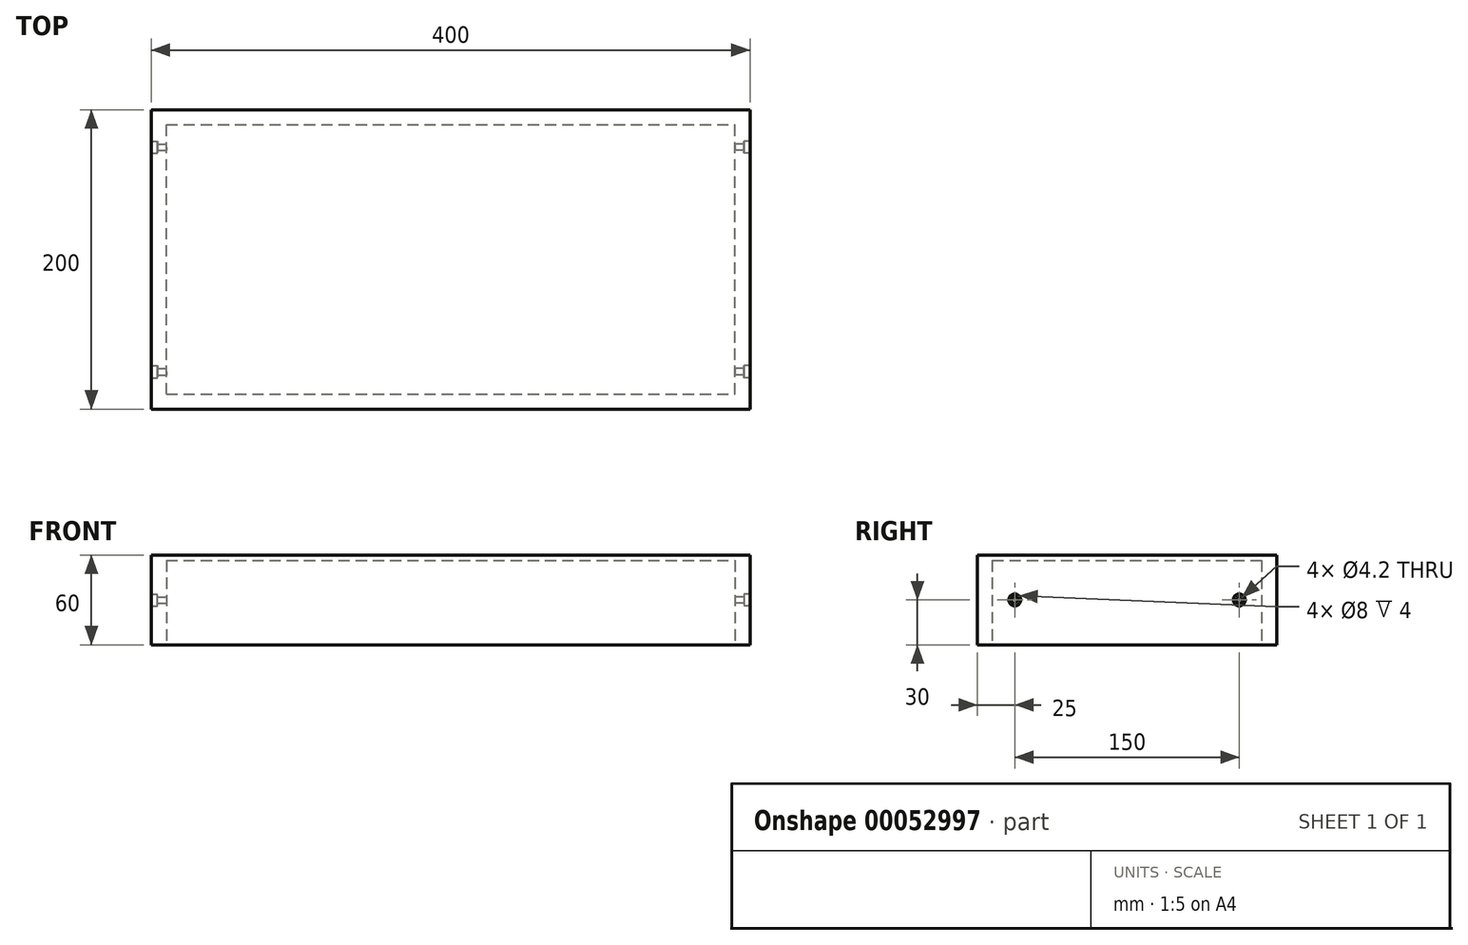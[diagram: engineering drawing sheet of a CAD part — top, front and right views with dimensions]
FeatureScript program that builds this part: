
annotation { "Feature Type Name" : "Feature", "Feature Type Description" : "" }
export const myFeature = defineFeature(function(context is Context, id is Id, definition is map)
    precondition{}
    {
        {
            var Q0;
            Q0=qCreatedBy(makeId("Top.planeOp"),FACE);
            var sketch = newSketch(context, id + "F0", { "sketchPlane" : qUnion([Q0])});
            skLineSegment(sketch, "E0.bottom", {"start": v(-200, 100) * mm, "end": v(200, 100) * mm});
            skLineSegment(sketch, "E0.top", {"start": v(-200, -100) * mm, "end": v(200, -100) * mm});
            skLineSegment(sketch, "E0.left", {"start": v(-200, 100) * mm, "end": v(-200, -100) * mm});
            skLineSegment(sketch, "E0.right", {"start": v(200, 100) * mm, "end": v(200, -100) * mm});
            skSolve(sketch);
        }
        {
            var Q0;
            Q0=makeQuery(id+"F0.imprint","IMPRINT",FACE,{"disambiguationData":[TD([[makeQuery(id+"F0.imprint","IMPRINT",EDGE,{"derivedFrom":sQuery(id+"F0.wireOp",EDGE,"E0.bottom")}),-1.0]])]});
            extrude(context, id + "F1", {"entities" : qUnion([Q0]), "oppositeDirection" : true, "depth" : 3.6 * mm});
        }
        {
            var Q0;
            Q0=makeQuery(id+"F1.opExtrude","CAP_FACE",FACE,{"disambiguationData":[OSD([sQuery(id+"F0.wireOp",EDGE,"E0.bottom"),sQuery(id+"F0.wireOp",EDGE,"E0.top"),sQuery(id+"F0.wireOp",EDGE,"E0.left"),sQuery(id+"F0.wireOp",EDGE,"E0.right")])],"isStart":true});
            cPlane(context, id + "F2", {"entities" : qUnion([Q0]), "cplaneType" : CPlaneType.OFFSET, "offset" : 60 * mm, "oppositeDirection" : true, "width" : 150 * mm, "height" : 150 * mm});
        }
        {
            var Q0;
            Q0=qCreatedBy(id+"F2.planeOp",FACE);
            var sketch = newSketch(context, id + "F3", { "sketchPlane" : qUnion([Q0])});
            skLineSegment(sketch, "E1.0", {"start": v(-200, 100) * mm, "end": v(-200, -100) * mm});
            skLineSegment(sketch, "E2.0", {"start": v(-200, -100) * mm, "end": v(200, -100) * mm});
            skLineSegment(sketch, "E3.0", {"start": v(200, 100) * mm, "end": v(200, -100) * mm});
            skLineSegment(sketch, "E4.0", {"start": v(-200, 100) * mm, "end": v(200, 100) * mm});
            skLineSegment(sketch, "E5.bottom", {"start": v(-190, -90) * mm, "end": v(190, -90) * mm});
            skLineSegment(sketch, "E5.top", {"start": v(-190, 90) * mm, "end": v(190, 90) * mm});
            skLineSegment(sketch, "E5.left", {"start": v(-190, -90) * mm, "end": v(-190, 90) * mm});
            skLineSegment(sketch, "E5.right", {"start": v(190, -90) * mm, "end": v(190, 90) * mm});
            skLineSegment(sketch, "E6", {"start": v(-190, -90) * mm, "end": v(-200, -90) * mm, "construction": true});
            skLineSegment(sketch, "E7", {"start": v(-190, -90) * mm, "end": v(-190, -100) * mm, "construction": true});
            skLineSegment(sketch, "E8", {"start": v(190, 90) * mm, "end": v(200, 90) * mm, "construction": true});
            skLineSegment(sketch, "E9", {"start": v(190, 90) * mm, "end": v(190, 100) * mm, "construction": true});
            skSolve(sketch);
        }
        {
            var Q0;
            Q0=makeQuery(id+"F3.imprint","IMPRINT",FACE,{"disambiguationData":[TD([[makeQuery(id+"F3.imprint","IMPRINT",EDGE,{"derivedFrom":sQuery(id+"F3.wireOp",EDGE,"E1.0")}),1.0]])]});
            var Q1;
            Q1=makeQuery(id+"F1.opExtrude","CAP_FACE",FACE,{"disambiguationData":[OSD([sQuery(id+"F0.wireOp",EDGE,"E0.bottom"),sQuery(id+"F0.wireOp",EDGE,"E0.top"),sQuery(id+"F0.wireOp",EDGE,"E0.left"),sQuery(id+"F0.wireOp",EDGE,"E0.right")])],"isStart":false});
            extrude(context, id + "F4", {"entities" : qUnion([Q0]), "operationType" : NewBodyOperationType.ADD, "endBound" : BoundingType.UP_TO_SURFACE, "endBoundEntityFace" : qUnion([Q1]), "depth" : 25 * mm});
        }
        {
            var Q0;
            Q0=makeQuery(id+"F4.boolean.opBoolean","MERGE",FACE,{"derivedFrom":[makeQuery(id+"F1.opExtrude","SWEPT_FACE",FACE,{"disambiguationData":[OSD([sQuery(id+"F0.wireOp",EDGE,"E0.right")])]}),makeQuery(id+"F4.opExtrude","SWEPT_FACE",FACE,{"disambiguationData":[OSD([sQuery(id+"F3.wireOp",EDGE,"E3.0")])]})]});
            var sketch = newSketch(context, id + "F5", { "sketchPlane" : qUnion([Q0])});
            skPoint(sketch, "E10", {"position": v(-75, -30) * mm});
            skPoint(sketch, "E11", {"position": v(75, -30) * mm});
            skLineSegment(sketch, "E12", {"start": v(100, -30) * mm, "end": v(-100, -30) * mm, "construction": true});
            skLineSegment(sketch, "E13", {"start": v(0, 0) * mm, "end": v(0, -60) * mm, "construction": true});
            skLineSegment(sketch, "E14", {"start": v(0, -60) * mm, "end": v(0, -30) * mm, "construction": true});
            skPoint(sketch, "E15", {"position": v(0, -30) * mm});
            skSolve(sketch);
        }
        {
            var Q0;
            Q0=makeQuery(id+"F4.boolean.opBoolean","MERGE",FACE,{"derivedFrom":[makeQuery(id+"F1.opExtrude","SWEPT_FACE",FACE,{"disambiguationData":[OSD([sQuery(id+"F0.wireOp",EDGE,"E0.left")])]}),makeQuery(id+"F4.opExtrude","SWEPT_FACE",FACE,{"disambiguationData":[OSD([sQuery(id+"F3.wireOp",EDGE,"E1.0")])]})]});
            var sketch = newSketch(context, id + "F6", { "sketchPlane" : qUnion([Q0])});
            skPoint(sketch, "E16", {"position": v(-75, -30) * mm});
            skPoint(sketch, "E17", {"position": v(75, -30) * mm});
            skLineSegment(sketch, "E18", {"start": v(0, 0) * mm, "end": v(0, -60) * mm, "construction": true});
            skLineSegment(sketch, "E19", {"start": v(-100, -30) * mm, "end": v(100, -30) * mm, "construction": true});
            skPoint(sketch, "E20", {"position": v(0, -30) * mm});
            skSolve(sketch);
        }
        {
            var Q0;
            Q0=sQuery(id+"F6.wireOp",VERTEX,"E16");
            var Q1;
            Q1=sQuery(id+"F6.wireOp",VERTEX,"E17");
            var Q2;
            Q2=sQuery(id+"F5.wireOp",VERTEX,"E11");
            var Q3;
            Q3=sQuery(id+"F5.wireOp",VERTEX,"E10");
            var Q4;
            Q4=makeQuery(id+"F1.opExtrude","SWEPT_BODY",BODY,{"disambiguationData":[OSD([sQuery(id+"F0.wireOp",EDGE,"E0.bottom"),sQuery(id+"F0.wireOp",EDGE,"E0.top"),sQuery(id+"F0.wireOp",EDGE,"E0.left"),sQuery(id+"F0.wireOp",EDGE,"E0.right")])]});
            hole(context, id + "F7", {"style" : HoleStyle.C_BORE, "endStyle" : HoleEndStyle.BLIND, "holeDiameter" : 4.2 * mm, "cBoreDiameter" : 8 * mm, "cBoreDepth" : 4 * mm, "majorDiameter" : 5 * mm, "holeDepth" : 12 * mm, "locations" : qUnion([Q0, Q1, Q2, Q3]), "scope" : qUnion([Q4]), "tappedDepth" : 12 * mm, "tapClearance" : 3, "startStyle" : HoleStartStyle.SKETCH});
        }
    });
